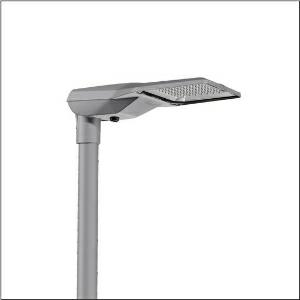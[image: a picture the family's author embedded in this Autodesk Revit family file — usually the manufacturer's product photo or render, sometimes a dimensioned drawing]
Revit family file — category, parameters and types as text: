
# Revit family: streetlight_sl_21_midi___p0_8a_5xe3u33r08mb_4c8c
name_source: partatom
category: Lighting Fixtures
units: mm (PartAtom-declared; Revit-internal decimal feet)

## family parameters
Cut with Voids When Loaded = No
Host = Face
Light Source = No
Part Type = Normal
Room Calculation Point = No
Round Connector Dimension = Use Diameter
Shared = No

## types (1)
- --- (1 x LED, 18430 lm, 136 W, 3000K)
    Apparent Load = 136 VA
    CIE Flux Codes = 33 69 96 100 100
    Color Rendering = 70
    Color Temperature = 3000K
    Default Elevation = 1800 mm
    Description = Streetlight SL 21 midi, mast luminaire, primary light control with lens, of PMMA, primary optical cover: cover, of toughened safety glass, transparent, light distribution: P0.8a, light emission: direct distribution, primary light characteristic: asymmetric, installation type: post-top, side-entry, LED, High Power LED, rated luminous flux: 18.430lm, luminous efficacy: 136lm/W, light colour: 730, colour temperature: 3000K, control gear: D4i, control: pre-setting: logarithmic dimming characteristic, flexible luminous flux parameterisation, time-dependent luminous flux control, constant luminous flux control, overheat protection, mains connection: 230..240V, AC, 50/60Hz, start of lifetime: 136W, end of service life: 142W, reduction: 61W, luminaire housing, of diecast aluminium, powder-coated, SITECO metallic grey (DB 702S), corrosivity category C5 high according to DIN EN ISO 12944, multi-level sealing system, sealing non-destructively replaceable, inclination adjustable: 0°, 5°, 10°, 15°, please order mast flange separately, length: 644mm, width: 335mm, height: 110mm, mast flange for spigot size: 42mm (side-entry): 5XC10008XM4, 60/48mm (side-entry/post-top): 5XC10108XM2, 76/60mm (side-entry/post-top): 5XC10108XM1, mounting height: 4..8m, Smart Interface below, protection rating (complete): IP66, insulation class (complete): insulation class II (safety insulation), certification: CE, ENEC, ENEC+, VDE, impact resistance: IK10, permissible operating ambient temperature for outdoor applications: -40..+50°C, standard-compliant lighting for roads and squares, packaging unit: 1 piece

Light Distribution: P0.8a
    Height = 111 mm
    Lamp = 1 x LED
    Lamp Light Flux = 18430 lm
    Lamp Power = 136 W
    Lamp count = 1
    Length = 644 mm
    Luminous efficacy = 136 lm/W
    Manufacturer = Siteco
    ModVariant = No
    Model = 5XE3U33R08MB
    Number of Poles = 1
    OnlyDefault = Yes
    Power Factor = 1
    Product Name = Streetlight SL 21 midi | P0.8a
    Product group = mast luminaire | pylon top
    ProductGroupID = 6100
    Protection Class = Protection class II
    Protection Degree = IP 66
    RLX_Detail_Level = 1
    RLX_Emergency_Light_Flux = 0 lm
    RLX_Emergency_Type = 0
    RLX_Emergency_Type_DB = No
    RlxData = <blob elided: 90701 chars, md5=71dd522d>
    Socket = socket
    Standby Power = 0 W
    System Light Flux = 18429 lm
    System Power = 136 W
    Type Comments = factory setting: luminous flux: 100 % | dim-lin: 254 | 695 mA
    Type Image = l_1004300.jpg
    URL = http://relux.com
    VarID = @adj_080403
    Voltage = 0 V
    Weight = 0.00 kg
    Width = 336 mm

## geometry (parser evidence)
native form markers: Blend x4, Sweep x12
no freeform markers — native parametric forms only
